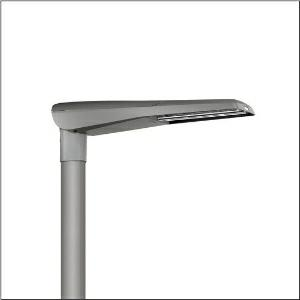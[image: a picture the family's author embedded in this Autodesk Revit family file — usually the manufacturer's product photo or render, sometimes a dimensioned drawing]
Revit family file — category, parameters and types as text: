
# Revit family: streetlight_sl_11_iq_mini___st1_2a_5xc2ac1f08he_c396
name_source: partatom
category: Lighting Fixtures
units: mm (PartAtom-declared; Revit-internal decimal feet)

## family parameters
Cut with Voids When Loaded = No
Host = Face
Light Source = No
Part Type = Normal
Room Calculation Point = No
Round Connector Dimension = Use Diameter
Shared = No

## types (1)
- --- (1 x LED, 6820 lm, 63.6 W, 2200K)
    Apparent Load = 64 VA
    CIE Flux Codes = 32 70 96 100 100
    Color Rendering = 70
    Color Temperature = 2200K
    Default Elevation = 1800 mm
    Description = Streetlight SL 11 iQ mini, mast luminaire, primary light control with 3 zone facetted reflector, of plastic, silver coated, highly specular, primary optical cover: cover, of PMMA, transparent, light distribution: ST1.2a, light emission: direct distribution, primary light characteristic: asymmetric, installation type: post-top, side-entry, lamps: LED, High Power LED, rated values: 8.330lm | 62,2W | 133,9lm/W (begin service life); end service life: 8.330lm | 65,6W; at 50% lumin. flux: 4.165lm | 29,4W | 141,7lm/W, colour temperature: 2200/2700/3000/4000K, colour rendering: CRI > 70, light colour: 722/727/730/740, light setting 1 begin service life: 100% | 8.330lm | 62,2W | 133,9lm/W | 3.000K, light setting 1 end service life: 65,6W, further light settings possible, control: Street-Remote, Auto-Match, Temp-Guard, Lumen-Switch, Night-Set, Smart-Wire, Light-Fading, Desk-Remote (wireless, voltage-free reading and setting of iQ features in the workshop via application-optimized NFC function/RFID function), optimised constant luminous flux control (CLO 2.0), with cable H07RN-F 5x 1.5mm², mains connection: 230..240V, AC, 50/60Hz, connection cable pre-assembled, cable length: 8,5m, luminaire housing, of diecast aluminium, powder-coated, Siteco® metallic grey (DB 702S), please order mast flange separately, inclination adjustable without tools: 0°, 5°, 10°, 15° (post-top) | 0°, -5°, -10°, -15° (side-entry), sealing non-destructively replaceable, multi-level sealing system, length: 736mm, width: 174mm, height: 116mm, mast flange for spigot size: 42mm (side-entry): 5XC10008XM4, 60/48mm (side-entry/post-top): 5XC10108XM2, 76/60mm (side-entry/post-top): 5XC10108XM1, equipment: Power, protection rating (complete): IP66, insulation class (complete): insulation class II (safety insulation), certification: CE, ENEC, ENEC+, VDE, impact resistance: IK10, permissible operating ambient temperature for outdoor applications: -25..+50°C, standard-compliant lighting for roads and squares, Environmental Product Declaration (EPD) tested and certified by an independent institute, packaging unit: 1 piece

Light Distribution: ST1.2a
    Height = 116 mm
    Lamp = 1 x LED
    Lamp Light Flux = 6820 lm
    Lamp Power = 63.6 W
    Lamp count = 1
    Length = 736 mm
    Luminous efficacy = 107 lm/W
    Manufacturer = Siteco
    ModVariant = No
    Model = 5XC2AC1F08HE
    Number of Poles = 1
    OnlyDefault = Yes
    Power Factor = 1
    Product Name = Streetlight SL 11 iQ mini | ST1.2a
    Product group = mast luminaire | pylon top
    ProductGroupID = 6100
    Protection Class = Protection class II
    Protection Degree = IP 66
    RLX_Detail_Level = 1
    RLX_Emergency_Light_Flux = 0 lm
    RLX_Emergency_Type = 0
    RLX_Emergency_Type_DB = No
    RlxData = <blob elided: 53797 chars, md5=61aea9e2>
    Socket = socket
    Standby Power = 0 W
    System Light Flux = 6820 lm
    System Power = 64 W
    Type Comments = individual setting: luminous flux: 100 % | dim-lin: 254 | 866 mA
    Type Image = l_1003508.jpg
    URL = http://relux.com
    VarID = @adj_034634
    Voltage = 0 V
    Weight = 0.00 kg
    Width = 174 mm

## geometry (parser evidence)
native form markers: Blend x4, Sweep x11
no freeform markers — native parametric forms only
